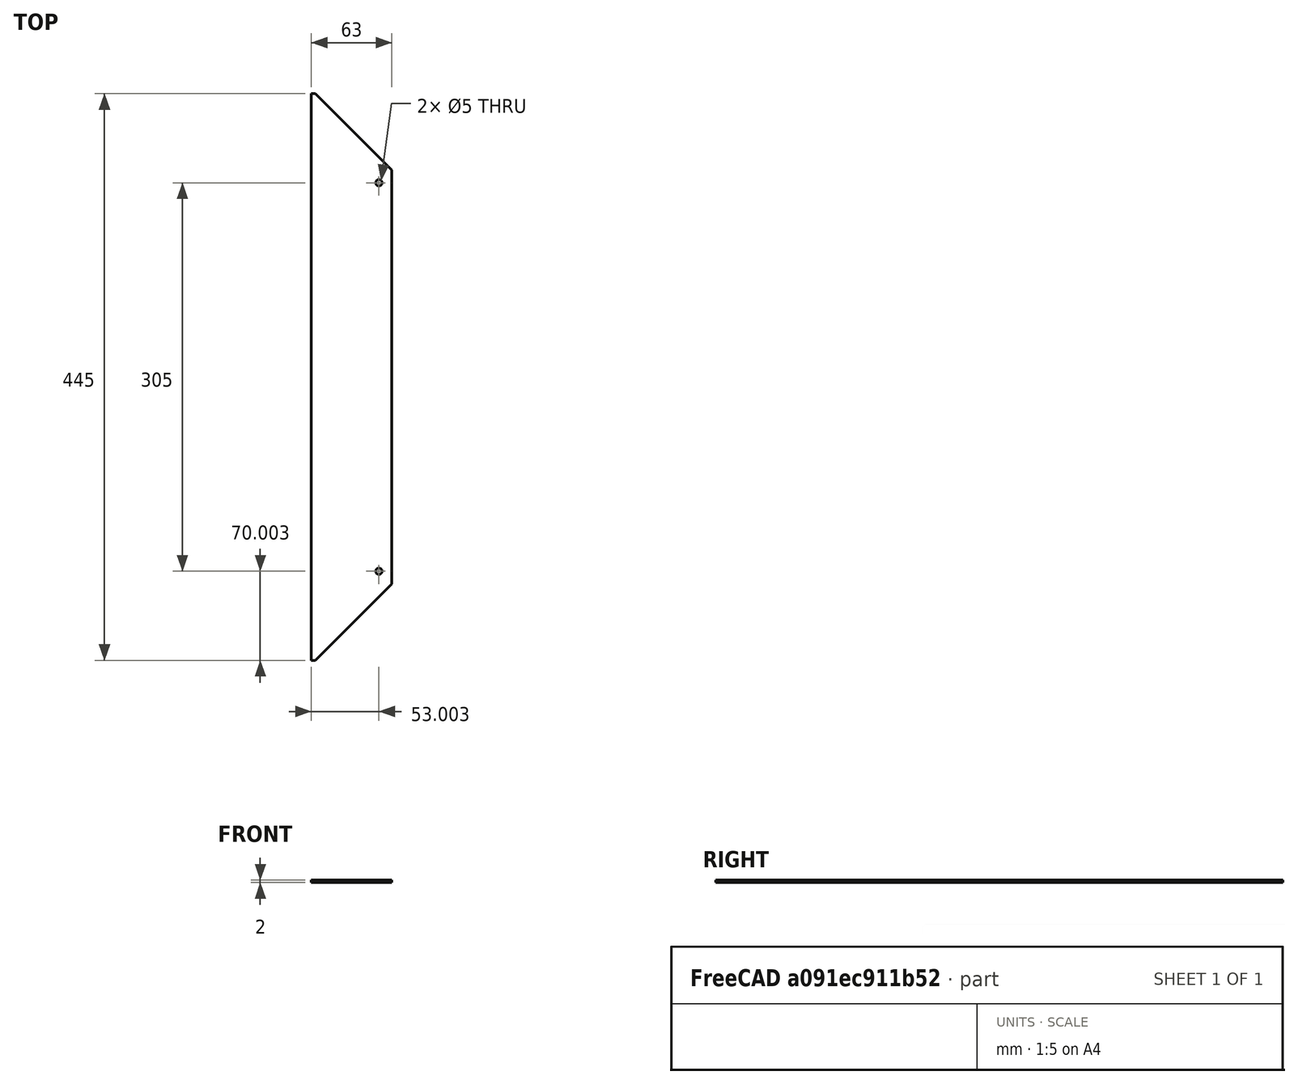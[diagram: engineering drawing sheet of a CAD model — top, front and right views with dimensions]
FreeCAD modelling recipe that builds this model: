
FCSTD DOCUMENT  (FreeCAD 0.16R6698 (Git))
Label: petite plaque sup equerre
License: All rights reserved
LicenseURL: http://en.wikipedia.org/wiki/All_rights_reserved
objects: Sketcher::SketchObject×1, PartDesign::Pad×1
note: 3 computed .brp shape members not serialized (recipe doc carries the construction recipe); baked Part::Feature solids carry a one-line shape summary decoded from their .brp

FEATURE [Sketcher::SketchObject] Sketch
  sketch-geometry (8):
    g0: LineSegment StartX=-32.7566 StartY=225.063 StartZ=0 EndX=-29.7566 EndY=225.063 EndZ=0
    g1: LineSegment StartX=30.2434 StartY=165.063 StartZ=0 EndX=30.2434 EndY=-159.937 EndZ=0
    g2: LineSegment StartX=-29.7566 StartY=-219.937 StartZ=0 EndX=-32.7566 EndY=-219.937 EndZ=0
    g3: LineSegment StartX=-32.7566 StartY=-219.937 StartZ=0 EndX=-32.7566 EndY=225.063 EndZ=0
    g4: LineSegment StartX=-29.7566 StartY=225.063 StartZ=0 EndX=30.2434 EndY=165.063 EndZ=0
    g5: LineSegment StartX=30.2434 StartY=-159.937 StartZ=0 EndX=-29.7566 EndY=-219.937 EndZ=0
    g6: Circle CenterX=20.2434 CenterY=155.063 CenterZ=0 NormalX=0 NormalY=0 NormalZ=1 Radius=2.5
    g7: Circle CenterX=20.2434 CenterY=-149.937 CenterZ=0 NormalX=0 NormalY=0 NormalZ=1 Radius=2.5
  constraints (22):
    c: Coincident(g2,g3)
    c: Coincident(g3,g0)
    c: Horizontal(g0)
    c: Horizontal(g2)
    c: Vertical(g1)
    c: Vertical(g3)
    c: Coincident(g4,g0)
    c: Coincident(g4,g1)
    c: Coincident(g5,g1)
    c: Coincident(g5,g2)
    c: DistanceX(g5,g5) = 60
    c: DistanceY(g5,g5) = 60
    c: DistanceX(g4,g4) = 60
    c: DistanceY(g4,g4) = 60
    c: DistanceX(g0,g0) = 3
    c: DistanceY(g1,g1) = 325
    c: Radius(g7) = 2.5
    c: Equal(g7,g6)
    c: DistanceX(g6,g1) = 10
    c: DistanceY(g6,g1) = 10
    c: DistanceY(g1,g7) = 10
    c: DistanceX(g7,g1) = 10
FEATURE [PartDesign::Pad] Pad
  Length = 2
  Length2 = 100
  Sketch = -> Sketch
  Type = 0
